# Revit family: Sanitary_Accessories_Svedholm_Unit
name_source: partatom
category: Furniture
revit_build: Autodesk Revit 2018 (Build: 20190510_1515(x64)
units: mm (PartAtom-declared; Revit-internal decimal feet)

## family parameters
Cut with Voids When Loaded = No
Host = Face
OmniClass Number = 23.21.11.00
OmniClass Title = Commercial Furniture
Room Calculation Point = No
Shared = No

## types (4) — shared parameters
BIMobject category = Shelving & Storage
Default Elevation = 1219 mm
Description = A shelf system made of perforated powder coated steel. Bookend made of powder coated wire.
Design country = Sweden
Edition number = 1
IFC Classification = Object
Manufacturer = Svedholm
Manufacturer country = Sweden
Manufacturer name = Svedholm
Material main = Powder coated steel
Model = Unit
OmniClass Code = 23-21 11 00
OmniClass Description = Commercial Furniture
Product Guid = d3ccd514-d06d-4ea8-b160-b10ea6b03f12
Product SKU = Unit
Product data url = https://bimobject.com
Product family = Unit
Product group = Storage
Product name = Unit
Product url = https://www.svedholm.se
QR code = https://bimobject.com
URL = https://www.svedholm.se
Uniclass 2015 Code = Zz_30_60
Uniclass 2015 Name = Objects

## per-type parameters (varying)
| type | Back plate | Book end | Left | Right |
| ART - (413.200.001.01) | No | No | No | Yes |
| ART - (413.200.001.02) | No | No | Yes | No |
| ART - (413.200.001.03) | No | Yes | No | No |
| ART - (413.200.003) | Yes | No | No | No |

## geometry (parser evidence)
native form markers: Sweep x4
no freeform markers — native parametric forms only
